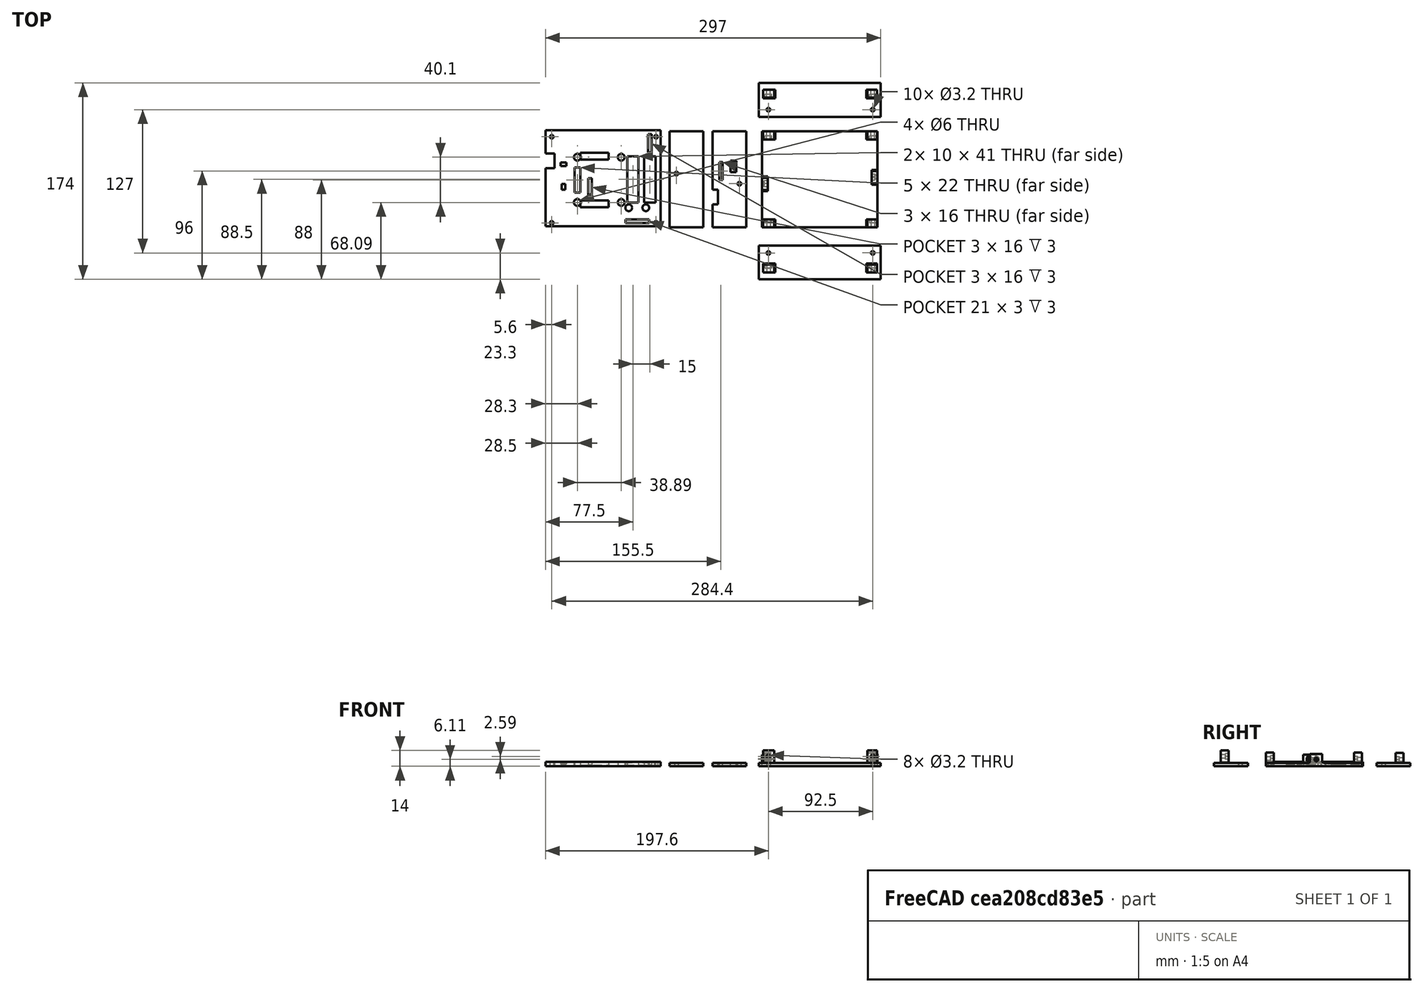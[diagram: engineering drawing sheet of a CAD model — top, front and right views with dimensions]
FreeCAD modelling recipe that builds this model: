
FCSTD DOCUMENT  (FreeCAD 0.16R6703 (Git))
Label: lightwand_box_for_printing
License: All rights reserved
LicenseURL: http://en.wikipedia.org/wiki/All_rights_reserved
objects: Part::Cylinder×31, Part::Box×30, Part::Cut×30, Part::MultiFuse×11, Part::Prism×10, Part::Chamfer×5, Mesh::Feature×1
note: 117 computed .brp shape members not serialized (recipe doc carries the construction recipe); baked Part::Feature solids carry a one-line shape summary decoded from their .brp

FEATURE [Mesh::Feature] lightwand
FEATURE [Part::Box] Box  label="Cube_top"
  Height = 4
  Length = 102
  Placement = pos=(-2,0,1) rot=(0,0,1;0rad)
  Width = 85
FEATURE [Part::Box] Box001  label="Cube_bottom"
  Height = 3
  Length = 102
  Placement = pos=(-2,0,-25) rot=(0,0,1;0rad)
  Width = 85
FEATURE [Part::Box] Box002  label="Cube_front"
  Height = 30
  Length = 3
  Placement = pos=(-5,0,-25) rot=(0,0,1;0rad)
  Width = 85
FEATURE [Part::Box] Box003  label="Cube_back"
  Height = 30
  Length = 3
  Placement = pos=(100,0,-25) rot=(0,0,1;0rad)
  Width = 85
FEATURE [Part::Box] Box004  label="Cube_right"
  Height = 30
  Length = 108
  Placement = pos=(-5,-3,-25) rot=(0,0,1;0rad)
  Width = 3
FEATURE [Part::Box] Box005  label="Cube_left"
  Height = 30
  Length = 108
  Placement = pos=(-5,85,-25) rot=(0,0,1;0rad)
  Width = 3
FEATURE [Part::Box] Box006  label="led array connector"
  Height = 10
  Length = 17
  Placement = pos=(-11,20.5,0) rot=(0,0,1;0rad)
  Width = 13
FEATURE [Part::Box] Box007  label="led array connector001"
  Height = 10
  Length = 17
  Placement = pos=(-11,20.5,0) rot=(0,0,1;0rad)
  Width = 13
FEATURE [Part::Box] Box008  label="USB connector002"
  Height = 5
  Length = 17
  Placement = pos=(-11,49,-16) rot=(0,0,1;0rad)
  Width = 10
FEATURE [Part::Cut] Cut001  label="top without led array connector"
  Base = -> Box
  Tool = -> Box006
FEATURE [Part::Box] Box009  label="button array"
  Height = 10
  Length = 10
  Placement = pos=(70.5,23,0) rot=(0,0,1;0rad)
  Width = 41
FEATURE [Part::Box] Box010  label="button array001"
  Height = 10
  Length = 10
  Placement = pos=(85.5,23,0) rot=(0,0,1;0rad)
  Width = 41
FEATURE [Part::MultiFuse] Fusion001  label="button arrays"
  Shapes = -> [Box010,Box009]
FEATURE [Part::Cut] Cut002
  Base = -> Cut001
  Tool = -> Fusion001
FEATURE [Part::Cylinder] Cylinder  label="screen hole 1"
  Angle = 360
  Height = 10
  Placement = pos=(26.3,23.81,0) rot=(0,0,1;0rad)
  Radius = 3
FEATURE [Part::Cylinder] Cylinder001  label="screen hole 002"
  Angle = 360
  Height = 10
  Placement = pos=(26.3,63.91,0) rot=(0,0,1;0rad)
  Radius = 3
FEATURE [Part::Cylinder] Cylinder002  label="screen hole 003"
  Angle = 360
  Height = 10
  Placement = pos=(65.19,23.81,0) rot=(0,0,1;0rad)
  Radius = 3
FEATURE [Part::Cylinder] Cylinder003  label="screen hole 004"
  Angle = 360
  Height = 10
  Placement = pos=(65.19,63.91,0) rot=(0,0,1;0rad)
  Radius = 3
FEATURE [Part::Box] Box011  label="screen_pin_connection"
  Height = 10
  Length = 5
  Placement = pos=(24,33,0) rot=(0,0,1;0rad)
  Width = 22
FEATURE [Part::MultiFuse] Fusion002  label="screen holes"
  Shapes = -> [Box011,Cylinder001,Cylinder002,Cylinder,Cylinder003]
FEATURE [Part::Cut] Cut003
  Base = -> Cut002
  Tool = -> Fusion002
FEATURE [Part::Box] Box012  label="pins_accelerometer"
  Height = 4
  Length = 21
  Placement = pos=(69,79,0) rot=(0,0,1;0rad)
  Width = 3
FEATURE [Part::Box] Box013  label="pins_bluetooth"
  Height = 4
  Length = 16
  Placement = pos=(92,3.5,0) rot=(0,0,1;1.5708rad)
  Width = 3
FEATURE [Part::Box] Box014  label="pins_sd card reader"
  Height = 4
  Length = 16
  Placement = pos=(39,42.5,0) rot=(0,0,1;1.5708rad)
  Width = 3
FEATURE [Part::Box] Box015  label="pins_TIVA 1"
  Height = 4
  Length = 25
  Placement = pos=(29,62,0) rot=(0,0,1;0rad)
  Width = 6
FEATURE [Part::Box] Box016  label="pins_TIVA 2"
  Height = 4
  Length = 25
  Placement = pos=(29,20,0) rot=(0,0,1;0rad)
  Width = 6
FEATURE [Part::Box] Box017  label="SMD resistor"
  Height = 3
  Length = 5
  Placement = pos=(11.5,28.5,0) rot=(0,0,1;0rad)
  Width = 3
FEATURE [Part::Box] Box018  label="SMD capacitor"
  Height = 3
  Length = 5
  Placement = pos=(15.5,47.5,0) rot=(0,0,1;1.5708rad)
  Width = 3
FEATURE [Part::Cylinder] Cylinder004  label="accelerometer screw 1"
  Angle = 360
  Height = 2
  Placement = pos=(86.99,68.6,0) rot=(0,0,1;0rad)
  Radius = 3
FEATURE [Part::Cylinder] Cylinder005  label="accelerometer screw 2"
  Angle = 360
  Height = 2
  Placement = pos=(71.83,68.6,0) rot=(0,0,1;0rad)
  Radius = 3
FEATURE [Part::Box] Box019  label="SD card reader"
  Height = 3
  Length = 6
  Placement = pos=(-8,42,-4) rot=(0,0,1;0rad)
  Width = 16
FEATURE [Part::MultiFuse] Fusion
  Shapes = -> [Box007,Box008,Box019]
FEATURE [Part::Cut] Cut  label="front"
  Base = -> Box002
  Tool = -> Fusion
FEATURE [Part::Cylinder] Cylinder006  label="board hole 1"
  Angle = 360
  Height = 10
  Placement = pos=(3.6,5.69,0) rot=(0,0,1;0rad)
  Radius = 1.6
FEATURE [Part::Cylinder] Cylinder007  label="board hole 2"
  Angle = 360
  Height = 10
  Placement = pos=(3.6,82,0) rot=(0,0,1;0rad)
  Radius = 1.6
FEATURE [Part::Cylinder] Cylinder008  label="board hole 3"
  Angle = 360
  Height = 10
  Placement = pos=(96,5.69,0) rot=(0,0,1;0rad)
  Radius = 1.6
FEATURE [Part::Cylinder] Cylinder009  label="board hole 4"
  Angle = 360
  Height = 10
  Placement = pos=(96,82,0) rot=(0,0,1;0rad)
  Radius = 1.6
FEATURE [Part::MultiFuse] Fusion004  label="board holes"
  Shapes = -> [Cylinder006,Cylinder008,Cylinder007,Cylinder009]
FEATURE [Part::MultiFuse] Fusion003  label="pins, SMDs and holes"
  Shapes = -> [Box012,Box014,Box018,Box013,Box015,Box016,Box017,Cylinder004,Cylinder005,Fusion004]
FEATURE [Part::Cylinder] Cylinder010  label="board hole 005"
  Angle = 360
  Height = 10
  Placement = pos=(3.6,5.69,0) rot=(0,0,1;0rad)
  Radius = 1.6
FEATURE [Part::Cylinder] Cylinder011  label="board hole 006"
  Angle = 360
  Height = 10
  Placement = pos=(3.6,82,0) rot=(0,0,1;0rad)
  Radius = 1.6
FEATURE [Part::Cylinder] Cylinder012  label="board hole 007"
  Angle = 360
  Height = 10
  Placement = pos=(96,5.69,0) rot=(0,0,1;0rad)
  Radius = 1.6
FEATURE [Part::Cylinder] Cylinder013  label="board hole 008"
  Angle = 360
  Height = 10
  Placement = pos=(96,82,0) rot=(0,0,1;0rad)
  Radius = 1.6
FEATURE [Part::MultiFuse] Fusion005  label="pins_SMDs and holes"
  Shapes = -> [Fusion003,Cylinder010,Cylinder012,Cylinder011,Cylinder013]
FEATURE [Part::Cut] Cut004  label="final top"
  Base = -> Cut003
  Placement = pos=(-192,86,5) rot=(1,0,0;3.14159rad)
  Tool = -> Fusion005
FEATURE [Part::Cylinder] Cylinder014  label="board hole 009"
  Angle = 360
  Height = 10
  Placement = pos=(3.6,5.69,-18.3) rot=(1,0,0;1.5708rad)
  Radius = 1.6
FEATURE [Part::Cylinder] Cylinder015  label="left hole 1"
  Angle = 360
  Height = 10
  Placement = pos=(3.6,82,-18.7) rot=(-1,0,0;1.5708rad)
  Radius = 1.6
FEATURE [Part::Cylinder] Cylinder016  label="board hole 011"
  Angle = 360
  Height = 10
  Placement = pos=(96,5.69,-18.4) rot=(1,0,0;1.5708rad)
  Radius = 1.6
FEATURE [Part::Cylinder] Cylinder017  label="left hole 2"
  Angle = 360
  Height = 10
  Placement = pos=(96,82,-18.7) rot=(-1,0,0;1.5708rad)
  Radius = 1.6
FEATURE [Part::Box] Box020  label="Cube"
  Height = 7
  Length = 10
  Placement = pos=(-1.25,0,-7) rot=(0,0,1;0rad)
  Width = 11
FEATURE [Part::Prism] Prism
  Circumradius = 3
  Height = 3
  Placement = pos=(3.6,5.69,-7) rot=(0,0,1;0rad)
  Polygon = 6
FEATURE [Part::Cut] Cut005
  Base = -> Box020
  Placement = pos=(0,0,-1) rot=(0,0,1;0rad)
  Tool = -> Prism
FEATURE [Part::Cut] Cut006  label="nut to board right 1"
  Base = -> Cut005
  Tool = -> Cylinder014
FEATURE [Part::Cylinder] Cylinder018  label="board hole 013"
  Angle = 360
  Height = 10
  Placement = pos=(3.6,5.69,-5) rot=(0,0,1;0rad)
  Radius = 1.6
FEATURE [Part::Box] Box021  label="Cube001"
  Height = 7
  Length = 8.5
  Placement = pos=(-1.25,0,-7) rot=(0,0,1;0rad)
  Width = 11
FEATURE [Part::Prism] Prism001
  Circumradius = 3
  Height = 3
  Placement = pos=(3.6,5.69,-7) rot=(0,0,1;0rad)
  Polygon = 6
FEATURE [Part::Cut] Cut007
  Base = -> Box021
  Placement = pos=(0,0,-1) rot=(0,0,1;0rad)
  Tool = -> Prism001
FEATURE [Part::Cut] Cut008  label="nut to board right 2"
  Base = -> Cut007
  Placement = pos=(92.5,0,0) rot=(0,0,1;0rad)
  Tool = -> Cylinder018
FEATURE [Part::Cylinder] Cylinder019  label="board hole 014"
  Angle = 360
  Height = 10
  Placement = pos=(3.6,5.69,-5) rot=(0,0,1;0rad)
  Radius = 1.6
FEATURE [Part::Box] Box022  label="Cube002"
  Height = 7
  Length = 10
  Placement = pos=(-1.25,0,-7) rot=(0,0,1;0rad)
  Width = 11
FEATURE [Part::Prism] Prism002
  Circumradius = 3
  Height = 3
  Placement = pos=(3.6,5.69,-7) rot=(0,0,1;0rad)
  Polygon = 6
FEATURE [Part::Cut] Cut009
  Base = -> Box022
  Placement = pos=(0,0,-1) rot=(0,0,1;0rad)
  Tool = -> Prism002
FEATURE [Part::Cut] Cut010  label="nut to board left 1"
  Base = -> Cut009
  Placement = pos=(0,76.2,0) rot=(0,0,1;0rad)
  Tool = -> Cylinder019
FEATURE [Part::Cylinder] Cylinder020  label="board hole 015"
  Angle = 360
  Height = 10
  Placement = pos=(3.6,5.69,-5) rot=(0,0,1;0rad)
  Radius = 1.6
FEATURE [Part::Box] Box023  label="Cube003"
  Height = 7
  Length = 8.5
  Placement = pos=(-1.25,0,-7) rot=(0,0,1;0rad)
  Width = 11
FEATURE [Part::Prism] Prism003
  Circumradius = 3
  Height = 3
  Placement = pos=(3.6,5.69,-7) rot=(0,0,1;0rad)
  Polygon = 6
FEATURE [Part::Cut] Cut011
  Base = -> Box023
  Placement = pos=(0,0,-1) rot=(0,0,1;0rad)
  Tool = -> Prism003
FEATURE [Part::Cut] Cut012  label="nut to board left 2"
  Base = -> Cut011
  Placement = pos=(92.5,76.2,0) rot=(0,0,1;0rad)
  Tool = -> Cylinder020
FEATURE [Part::Cylinder] Cylinder021  label="board hole 016"
  Angle = 360
  Height = 10
  Placement = pos=(3.6,5.69,-5) rot=(0,0,1;0rad)
  Radius = 1.6
FEATURE [Part::Box] Box024  label="Cube004"
  Height = 7
  Length = 8.5
  Placement = pos=(-1.25,0,-7) rot=(0,0,1;0rad)
  Width = 11
FEATURE [Part::Prism] Prism004
  Circumradius = 3
  Height = 3
  Placement = pos=(3.6,5.69,-7) rot=(0,0,1;0rad)
  Polygon = 6
FEATURE [Part::Cut] Cut013
  Base = -> Box024
  Placement = pos=(0,0,-1) rot=(0,0,1;0rad)
  Tool = -> Prism004
FEATURE [Part::Cut] Cut014  label="nut to board left 3"
  Base = -> Cut013
  Placement = pos=(92.5,86,-13) rot=(-1,0,0;1.5708rad)
  Tool = -> Cylinder021
FEATURE [Part::Cylinder] Cylinder022  label="board hole 017"
  Angle = 360
  Height = 10
  Placement = pos=(3.6,5.69,-5) rot=(0,0,1;0rad)
  Radius = 1.6
FEATURE [Part::Box] Box025  label="Cube005"
  Height = 7
  Length = 10
  Placement = pos=(-1.25,0,-7) rot=(0,0,1;0rad)
  Width = 11
FEATURE [Part::Prism] Prism005
  Circumradius = 3
  Height = 3
  Placement = pos=(3.6,5.69,-7) rot=(0,0,1;0rad)
  Polygon = 6
FEATURE [Part::Cut] Cut015
  Base = -> Box025
  Placement = pos=(0,0,-1) rot=(0,0,1;0rad)
  Tool = -> Prism005
FEATURE [Part::Cut] Cut016  label="nut to board left 4"
  Base = -> Cut015
  Placement = pos=(0,86,-13) rot=(-1,0,0;1.5708rad)
  Tool = -> Cylinder022
FEATURE [Part::Cylinder] Cylinder023  label="board hole 018"
  Angle = 360
  Height = 10
  Placement = pos=(3.6,5.69,-5) rot=(0,0,1;0rad)
  Radius = 1.6
FEATURE [Part::Box] Box026  label="Cube006"
  Height = 7
  Length = 8.5
  Placement = pos=(-1.25,0,-7) rot=(0,0,1;0rad)
  Width = 11
FEATURE [Part::Prism] Prism006
  Circumradius = 3
  Height = 3
  Placement = pos=(3.6,5.69,-7) rot=(0,0,1;0rad)
  Polygon = 6
FEATURE [Part::Cut] Cut017
  Base = -> Box026
  Placement = pos=(0,0,-1) rot=(0,0,1;0rad)
  Tool = -> Prism006
FEATURE [Part::Cut] Cut018  label="nut to board right 3"
  Base = -> Cut017
  Placement = pos=(92.5,-1,-24) rot=(1,0,0;1.5708rad)
  Tool = -> Cylinder023
FEATURE [Part::Cylinder] Cylinder024  label="board hole 019"
  Angle = 360
  Height = 10
  Placement = pos=(3.6,5.69,-5) rot=(0,0,1;0rad)
  Radius = 1.6
FEATURE [Part::Box] Box027  label="Cube007"
  Height = 7
  Length = 10
  Placement = pos=(-1.25,0,-7) rot=(0,0,1;0rad)
  Width = 11
FEATURE [Part::Prism] Prism007
  Circumradius = 3
  Height = 3
  Placement = pos=(3.6,5.69,-7) rot=(0,0,1;0rad)
  Polygon = 6
FEATURE [Part::Cut] Cut019
  Base = -> Box027
  Placement = pos=(0,0,-1) rot=(0,0,1;0rad)
  Tool = -> Prism007
FEATURE [Part::Cut] Cut020  label="nut to board right 4"
  Base = -> Cut019
  Placement = pos=(0,-1,-24) rot=(1,0,0;1.5708rad)
  Tool = -> Cylinder024
FEATURE [Part::Cylinder] Cylinder025  label="board hole 020"
  Angle = 360
  Height = 10
  Placement = pos=(3.6,5.69,-5) rot=(0,0,1;0rad)
  Radius = 1.6
FEATURE [Part::Box] Box028  label="Cube008"
  Height = 5
  Length = 9
  Placement = pos=(-1.25,0,-7) rot=(0,0,1;0rad)
  Width = 11
FEATURE [Part::Prism] Prism008
  Circumradius = 3
  Height = 3
  Placement = pos=(3.6,5.69,-7) rot=(0,0,1;0rad)
  Polygon = 6
FEATURE [Part::Cut] Cut021
  Base = -> Box028
  Placement = pos=(0,0,-1) rot=(0,0,1;0rad)
  Tool = -> Prism008
FEATURE [Part::Cut] Cut022  label="nut to front"
  Base = -> Cut021
  Placement = pos=(-5,33,-22.5) rot=(0,-1,0;1.5708rad)
  Tool = -> Cylinder025
FEATURE [Part::Cylinder] Cylinder026  label="front hole"
  Angle = 360
  Height = 10
  Placement = pos=(-7.4,38.69,-18.9) rot=(0,1,0;1.5708rad)
  Radius = 1.6
FEATURE [Part::Cylinder] Cylinder027  label="board hole 022"
  Angle = 360
  Height = 10
  Placement = pos=(3.6,5.69,-5) rot=(0,0,1;0rad)
  Radius = 1.6
FEATURE [Part::Box] Box029  label="Cube009"
  Height = 5
  Length = 9
  Placement = pos=(-1.25,0,-7) rot=(0,0,1;0rad)
  Width = 11
FEATURE [Part::Prism] Prism009
  Circumradius = 3
  Height = 3
  Placement = pos=(3.6,5.69,-7) rot=(0,0,1;0rad)
  Polygon = 6
FEATURE [Part::Cut] Cut023
  Base = -> Box029
  Placement = pos=(0,0,-1) rot=(0,0,1;0rad)
  Tool = -> Prism009
FEATURE [Part::Cut] Cut024  label="nut to back"
  Base = -> Cut023
  Placement = pos=(103,38,-14.5) rot=(0,1,0;1.5708rad)
  Tool = -> Cylinder027
FEATURE [Part::Cylinder] Cylinder028  label="back hole"
  Angle = 360
  Height = 10
  Placement = pos=(97.6,47.69,-18.9) rot=(0,1,0;1.5708rad)
  Radius = 1.6
FEATURE [Part::Cut] Cut025  label="final back"
  Base = -> Box003
  Placement = pos=(-59,0,103) rot=(0,1,0;1.5708rad)
  Tool = -> Cylinder028
FEATURE [Part::MultiFuse] Fusion006  label="left holes"
  Shapes = -> [Cylinder015,Cylinder017]
FEATURE [Part::Cut] Cut026  label="left side final"
  Base = -> Box005
  Tool = -> Fusion006
FEATURE [Part::Cut] Cut027  label="final front"
  Base = -> Cut
  Placement = pos=(-41,0,5) rot=(0,-1,0;1.5708rad)
  Tool = -> Cylinder026
FEATURE [Part::MultiFuse] Fusion007  label="bottom with nut holders"
  Shapes = -> [Cut024,Cut022,Cut014,Cut016,Cut020,Cut018,Box001]
FEATURE [Part::Cylinder] Cylinder029  label="board hole 023"
  Angle = 360
  Height = 10
  Placement = pos=(3.6,5.69,-18.3) rot=(1,0,0;1.5708rad)
  Radius = 1.6
FEATURE [Part::MultiFuse] Fusion010
  Shapes = -> [Cylinder016,Cylinder029]
FEATURE [Part::Cut] Cut028  label="right with holes"
  Base = -> Box004
  Tool = -> Fusion010
FEATURE [Part::MultiFuse] Fusion011  label="right side"
  Shapes = -> [Cut006,Cut008,Cut028]
FEATURE [Part::MultiFuse] Fusion012  label="left side"
  Shapes = -> [Cut026,Cut010,Cut012]
FEATURE [Part::Chamfer] Chamfer  label="bottom"
  Base = -> Fusion007
  Edges = 8 edges r=1: [Edge2,Edge4,Edge9,Edge11,Edge16,Edge22,Edge27,Edge29]
  Placement = pos=(0,0,25) rot=(0,0,1;0rad)
FEATURE [Part::Chamfer] Chamfer001
  Base = -> Fusion012
  Edges = 2 edges r=1: [Edge12,Edge16]
FEATURE [Part::Chamfer] Chamfer002
  Base = -> Chamfer001
  Edges = 1 edges r=0.5: [Edge6]
FEATURE [Part::Chamfer] Chamfer003  label="left side001"
  Base = -> Chamfer002
  Edges = 1 edges r=0.5: [Edge20]
  Placement = pos=(0,123,88) rot=(-1,0,0;1.5708rad)
FEATURE [Part::Chamfer] Chamfer004  label="right side001"
  Base = -> Fusion011
  Edges = 4 edges r=1: [Edge6,Edge19,Edge26,Edge27]
  Placement = pos=(0,-41,3) rot=(1,0,0;1.5708rad)
FEATURE [Part::Cylinder] Cylinder030  label="board hole 024"
  Angle = 360
  Height = 10
  Placement = pos=(3.6,-31.31,8.7) rot=(1,0,0;1.5708rad)
  Radius = 1.6
FEATURE [Part::Cut] Cut029
  Base = -> Chamfer004
  Tool = -> Cylinder030
